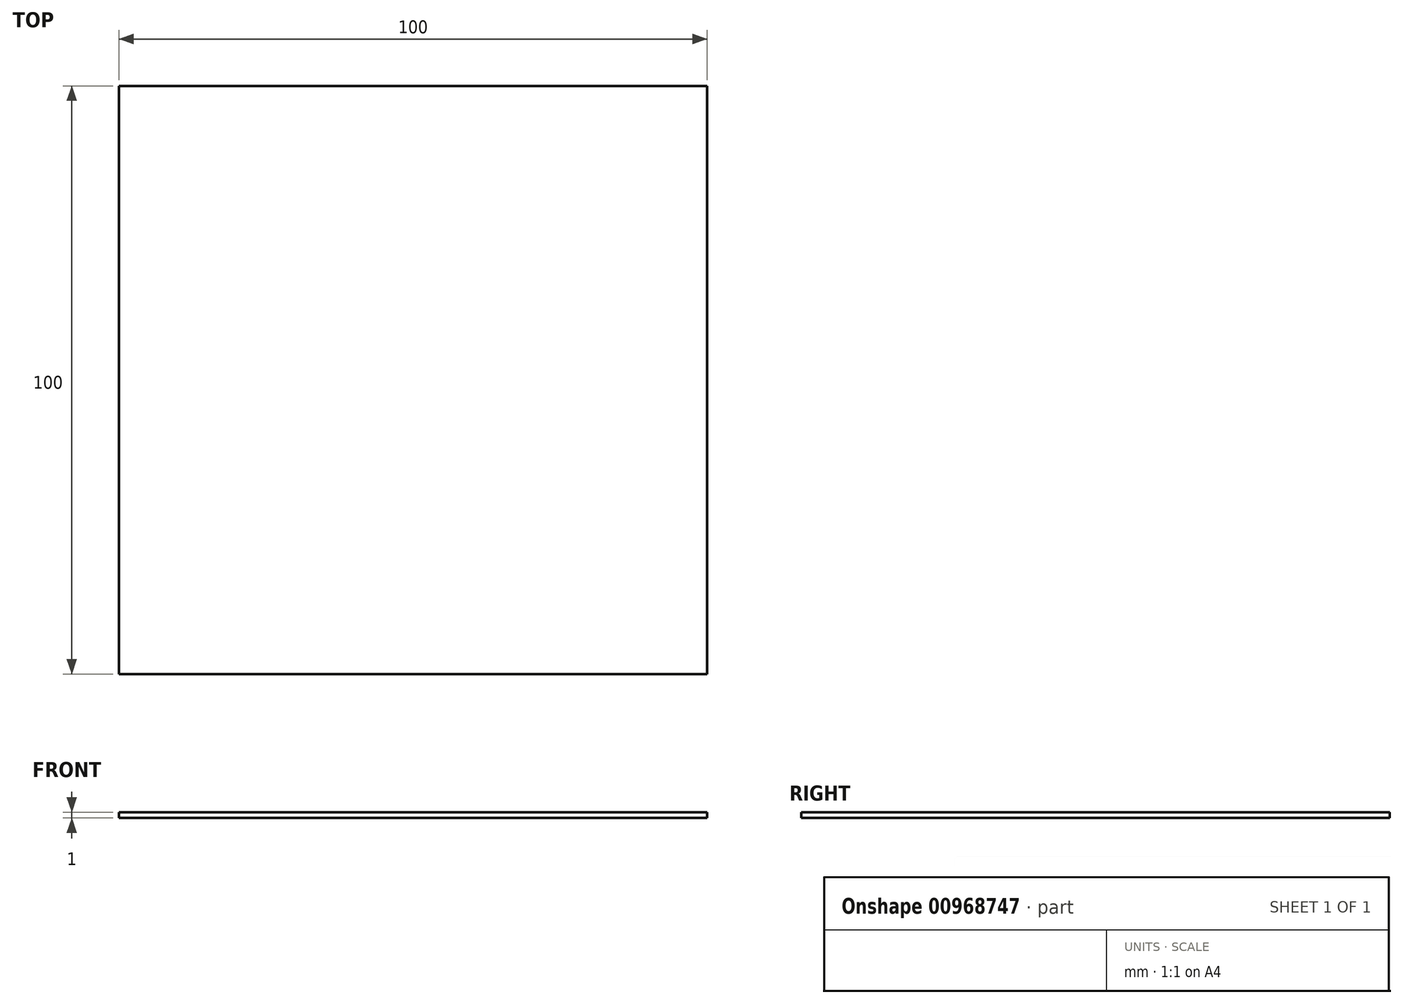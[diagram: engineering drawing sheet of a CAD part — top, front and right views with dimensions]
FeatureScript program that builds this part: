
annotation { "Feature Type Name" : "Feature", "Feature Type Description" : "" }
export const myFeature = defineFeature(function(context is Context, id is Id, definition is map)
    precondition{}
    {
        {
            var Q0;
            Q0=qCreatedBy(makeId("Top.planeOp"),FACE);
            var sketch = newSketch(context, id + "F0", { "sketchPlane" : qUnion([Q0])});
            skLineSegment(sketch, "E0.bottom", {"start": v(50, 50) * mm, "end": v(-50, 50) * mm});
            skLineSegment(sketch, "E0.top", {"start": v(50, -50) * mm, "end": v(-50, -50) * mm});
            skLineSegment(sketch, "E0.left", {"start": v(50, 50) * mm, "end": v(50, -50) * mm});
            skLineSegment(sketch, "E0.right", {"start": v(-50, 50) * mm, "end": v(-50, -50) * mm});
            skPoint(sketch, "E0.middle", {"position": v(0, 0) * mm});
            skSolve(sketch);
        }
        {
            var Q0;
            Q0 = qSketchRegion(id + "F0", true);
            extrude(context, id + "F1", {"entities" : qUnion([Q0]), "depth" : 1 * mm, "offsetDistance" : 25 * mm});
        }
    });
